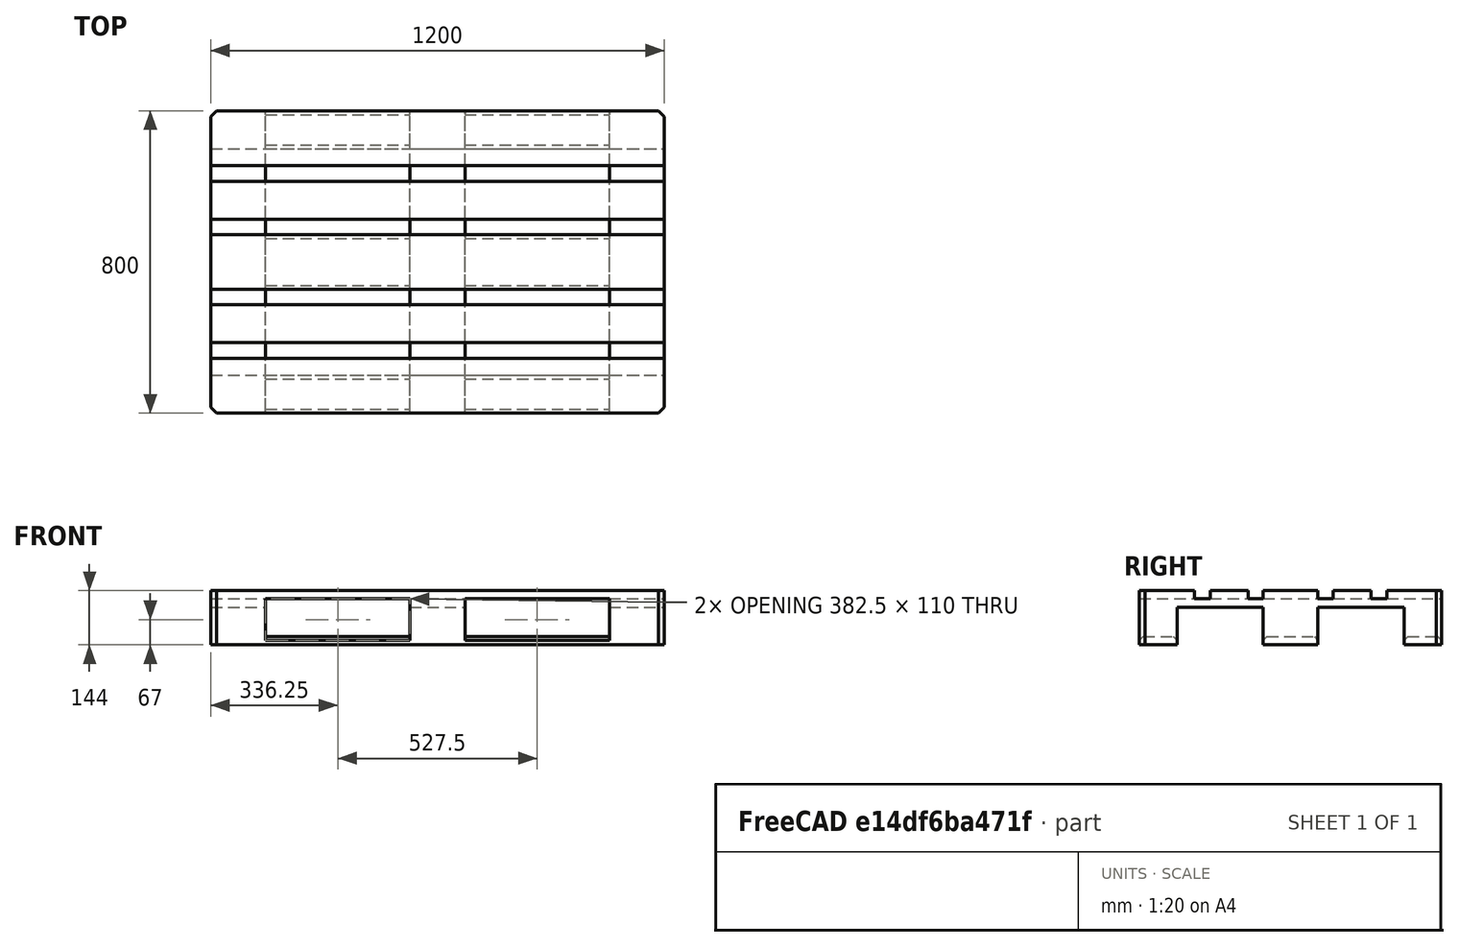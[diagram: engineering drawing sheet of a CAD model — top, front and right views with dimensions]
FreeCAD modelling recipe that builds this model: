
FCSTD DOCUMENT
Label: Pallet_EUR_1
objects: Part::Box×9, Part::MultiFuse×4, Part::Chamfer×2, Part::Cut×1
note: 16 computed .brp shape members not serialized (recipe doc carries the construction recipe); baked Part::Feature solids carry a one-line shape summary decoded from their .brp

FEATURE [Part::Box] Box
  Height = 144
  Length = 1200
  Width = 800
FEATURE [Part::Box] Box001
  Height = 100
  Length = 1200
  Placement = pos=(0,100,0) rot=(0,0,1;0rad)
  Width = 227.5
FEATURE [Part::Box] Box003
  Height = 100
  Length = 382.5
  Placement = pos=(145,0,22) rot=(0,0,1;0rad)
  Width = 800
FEATURE [Part::Box] Box004
  Height = 100
  Length = 382.5
  Placement = pos=(672.5,0,22) rot=(0,0,1;0rad)
  Width = 800
FEATURE [Part::MultiFuse] Fusion
  Shapes = -> [Box003,Box004]
FEATURE [Part::Box] Box005
  Height = 22
  Length = 1200
  Placement = pos=(0,472.5,122) rot=(0,0,1;0rad)
  Width = 40
FEATURE [Part::Box] Box006
  Height = 22
  Length = 1200
  Placement = pos=(0,287.5,122) rot=(0,0,1;0rad)
  Width = 40
FEATURE [Part::Box] Box007
  Height = 22
  Length = 1200
  Placement = pos=(0,613,122) rot=(0,0,1;0rad)
  Width = 42
FEATURE [Part::Box] Box008
  Height = 22
  Length = 1200
  Placement = pos=(0,145,122) rot=(0,0,1;0rad)
  Width = 42
FEATURE [Part::MultiFuse] Fusion003
  Shapes = -> [Box005,Box006,Box007,Box008]
FEATURE [Part::Box] Box009
  Height = 100
  Length = 1200
  Placement = pos=(0,472.5,0) rot=(0,0,1;0rad)
  Width = 227.5
FEATURE [Part::MultiFuse] Fusion004
  Shapes = -> [Box001,Box009]
FEATURE [Part::MultiFuse] Fusion005
  Shapes = -> [Fusion003,Fusion004,Fusion]
FEATURE [Part::Cut] Cut  label="EP_roh"
  Base = -> Box
  Tool = -> Fusion005
FEATURE [Part::Chamfer] Chamfer  label="Europalette"
  Base = -> Cut
  Edges = 4 edges r=15: [Edge80,Edge81,Edge119,Edge120]
  Placement = pos=(0,0,-144) rot=(0,0,1;0rad)
FEATURE [Part::Chamfer] Chamfer007  label="EuropaletteCham"
  Base = -> Chamfer
  Edges = 12 edges r=10: [Edge7,Edge11,Edge46,Edge86,Edge164,Edge166,Edge167,Edge172,Edge179,Edge181,Edge184,Edge193]
